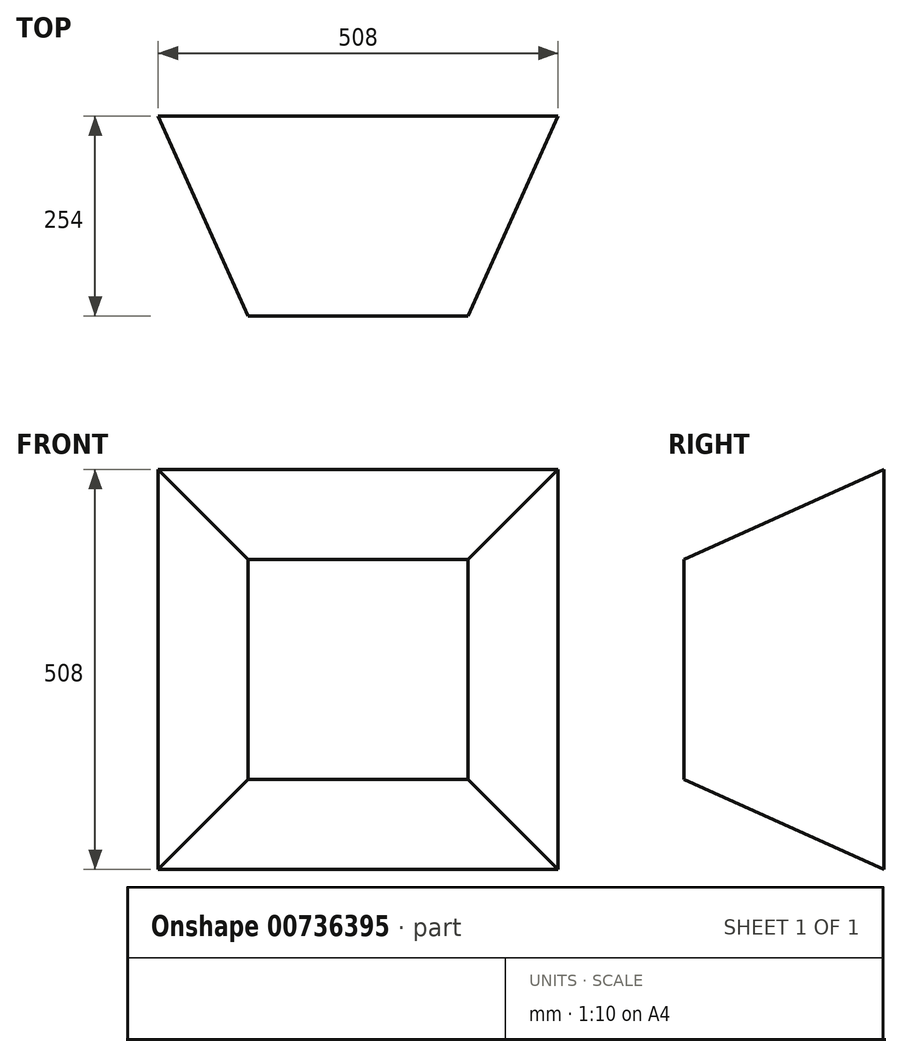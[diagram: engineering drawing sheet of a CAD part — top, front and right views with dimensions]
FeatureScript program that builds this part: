
annotation { "Feature Type Name" : "Feature", "Feature Type Description" : "" }
export const myFeature = defineFeature(function(context is Context, id is Id, definition is map)
    precondition{}
    {
        {
            var Q0;
            Q0=qCreatedBy(makeId("Front.planeOp"),FACE);
            var sketch = newSketch(context, id + "F0", { "sketchPlane" : qUnion([Q0])});
            skLineSegment(sketch, "E0.bottom", {"start": v(0, 0) * mm, "end": v(508, 0) * mm});
            skLineSegment(sketch, "E0.top", {"start": v(0, 508) * mm, "end": v(508, 508) * mm});
            skLineSegment(sketch, "E0.left", {"start": v(0, 0) * mm, "end": v(0, 508) * mm});
            skLineSegment(sketch, "E0.right", {"start": v(508, 0) * mm, "end": v(508, 508) * mm});
            skSolve(sketch);
        }
        {
            var Q0;
            Q0=makeQuery(id+"F0.imprint","IMPRINT",FACE,{"disambiguationData":[TD([[makeQuery(id+"F0.imprint","IMPRINT",EDGE,{"derivedFrom":sQuery(id+"F0.wireOp",EDGE,"E0.bottom")}),1.0]])]});
            extrude(context, id + "F1", {"entities" : qUnion([Q0]), "depth" : 254 * mm, "offsetDistance" : 25.4 * mm});
        }
        {
            var Q0;
            Q0=makeQuery(id+"F1.opExtrude","SWEPT_FACE",FACE,{"disambiguationData":[OSD([sQuery(id+"F0.wireOp",EDGE,"E0.right")])]});
            var sketch = newSketch(context, id + "F2", { "sketchPlane" : qUnion([Q0])});
            skLineSegment(sketch, "E1", {"start": v(0, 0) * mm, "end": v(0, 254) * mm, "construction": true});
            skLineSegment(sketch, "E2", {"start": v(0, 254) * mm, "end": v(-254, 254) * mm, "construction": true});
            skLineSegment(sketch, "E3", {"start": v(-254, 254) * mm, "end": v(-254, 393.7) * mm, "construction": true});
            skLineSegment(sketch, "E4", {"start": v(-254, 393.7) * mm, "end": v(0, 393.7) * mm, "construction": true});
            skLineSegment(sketch, "E5", {"start": v(0, 393.7) * mm, "end": v(0, 254) * mm, "construction": true});
            skLineSegment(sketch, "E6.MirrorCS", {"start": v(-254, 114.3) * mm, "end": v(0, 114.3) * mm, "construction": true});
            skLineSegment(sketch, "E7.MirrorCS", {"start": v(-254, 254) * mm, "end": v(-254, 114.3) * mm, "construction": true});
            skLineSegment(sketch, "E8", {"start": v(-254, 393.7) * mm, "end": v(0, 508) * mm});
            skLineSegment(sketch, "E9.MirrorCS", {"start": v(-254, 114.3) * mm, "end": v(0, 0) * mm});
            skSolve(sketch);
        }
        {
            var Q0;
            Q0 = qSketchRegion(id + "F2", true);
            var Q1;
            {var subQ0=sQuery(id+"F2.wireOp",EDGE,"E8");Q1=makeQuery(id+"F2.imprint","IMPRINT",FACE,{"disambiguationData":[TD([[makeQuery(id+"F2.imprint","IMPRINT",EDGE,{"derivedFrom":subQ0}),1.0]])]});}
            var Q2;
            {var subQ0=sQuery(id+"F2.wireOp",EDGE,"E9.MirrorCS");Q2=makeQuery(id+"F2.imprint","IMPRINT",FACE,{"disambiguationData":[TD([[makeQuery(id+"F2.imprint","IMPRINT",EDGE,{"derivedFrom":subQ0}),-1.0]])]});}
            extrude(context, id + "F3", {"entities" : qUnion([Q0, Q1, Q2]), "operationType" : NewBodyOperationType.REMOVE, "endBound" : BoundingType.THROUGH_ALL, "oppositeDirection" : true, "depth" : 25.4 * mm, "offsetDistance" : 25.4 * mm});
        }
        {
            var Q0;
            Q0=qCreatedBy(makeId("Top.planeOp"),FACE);
            var sketch = newSketch(context, id + "F4", { "sketchPlane" : qUnion([Q0])});
            skLineSegment(sketch, "E10", {"start": v(0, 0) * mm, "end": v(508, 0) * mm, "construction": true});
            skLineSegment(sketch, "E11", {"start": v(508, -254) * mm, "end": v(0, -254) * mm});
            skLineSegment(sketch, "E12", {"start": v(0, -254) * mm, "end": v(0, 0) * mm});
            skLineSegment(sketch, "E13", {"start": v(254, -254) * mm, "end": v(254, 0) * mm, "construction": true});
            skLineSegment(sketch, "E14.bottom", {"start": v(393.7, 0) * mm, "end": v(114.3, 0) * mm, "construction": true});
            skLineSegment(sketch, "E14.top", {"start": v(393.7, -254) * mm, "end": v(114.3, -254) * mm, "construction": true});
            skLineSegment(sketch, "E14.left", {"start": v(393.7, 0) * mm, "end": v(393.7, -254) * mm, "construction": true});
            skLineSegment(sketch, "E14.right", {"start": v(114.3, 0) * mm, "end": v(114.3, -254) * mm, "construction": true});
            skPoint(sketch, "E14.middle", {"position": v(254, -127) * mm});
            skLineSegment(sketch, "E15", {"start": v(0, 0) * mm, "end": v(114.3, -254) * mm});
            skLineSegment(sketch, "E16", {"start": v(393.7, -254) * mm, "end": v(508, 0) * mm});
            skLineSegment(sketch, "E17", {"start": v(508, -254) * mm, "end": v(542.02, -254) * mm});
            skLineSegment(sketch, "E18", {"start": v(542.02, -254) * mm, "end": v(542.02, 0) * mm});
            skLineSegment(sketch, "E19", {"start": v(542.02, 0) * mm, "end": v(508, 0) * mm});
            skSolve(sketch);
        }
        {
            var Q0;
            {var subQ0=sQuery(id+"F4.wireOp",EDGE,"E12");Q0=makeQuery(id+"F4.imprint","IMPRINT",FACE,{"disambiguationData":[TD([[makeQuery(id+"F4.imprint","IMPRINT",EDGE,{"derivedFrom":subQ0}),-1.0]])]});}
            var Q1;
            {var subQ0=sQuery(id+"F4.wireOp",EDGE,"E16");Q1=makeQuery(id+"F4.imprint","IMPRINT",FACE,{"disambiguationData":[TD([[makeQuery(id+"F4.imprint","IMPRINT",EDGE,{"derivedFrom":subQ0}),-1.0]])]});}
            extrude(context, id + "F5", {"entities" : qUnion([Q0, Q1]), "operationType" : NewBodyOperationType.REMOVE, "depth" : 508 * mm, "offsetDistance" : 25.4 * mm});
        }
    });
